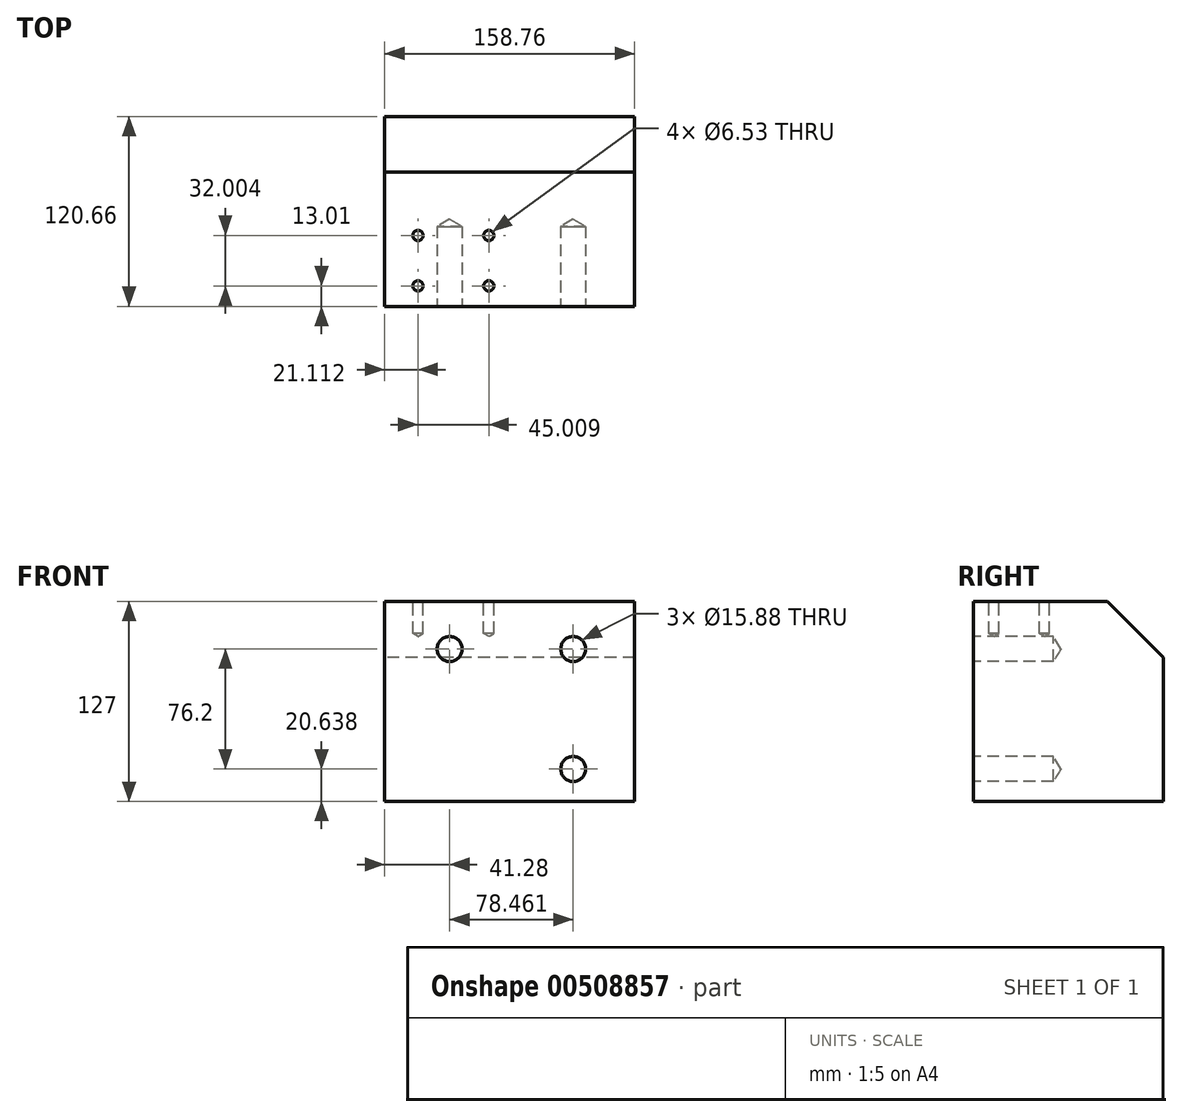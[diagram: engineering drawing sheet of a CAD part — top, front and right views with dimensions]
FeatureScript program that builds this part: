
annotation { "Feature Type Name" : "Feature", "Feature Type Description" : "" }
export const myFeature = defineFeature(function(context is Context, id is Id, definition is map)
    precondition{}
    {
        {
            var Q0;
            Q0=qCreatedBy(makeId("Right.planeOp"),FACE);
            var sketch = newSketch(context, id + "F0", { "sketchPlane" : qUnion([Q0])});
            skLineSegment(sketch, "E0.bottom", {"start": v(24.84, 63.5) * mm, "end": v(-60.32, 63.5) * mm});
            skLineSegment(sketch, "E0.top", {"start": v(60.32, -63.5) * mm, "end": v(-60.33, -63.5) * mm});
            skLineSegment(sketch, "E0.left", {"start": v(60.32, 28.02) * mm, "end": v(60.32, -63.5) * mm});
            skLineSegment(sketch, "E0.right", {"start": v(-60.32, 63.5) * mm, "end": v(-60.33, -63.5) * mm});
            skPoint(sketch, "E0.middle", {"position": v(0, 0) * mm});
            skLineSegment(sketch, "E1", {"start": v(24.84, 63.5) * mm, "end": v(60.32, 28.02) * mm});
            skSolve(sketch);
        }
        {
            var Q0;
            Q0=makeQuery(id+"F0.imprint","IMPRINT",FACE,{"disambiguationData":[TD([[makeQuery(id+"F0.imprint","IMPRINT",EDGE,{"derivedFrom":sQuery(id+"F0.wireOp",EDGE,"E0.bottom")}),1.0]])]});
            extrude(context, id + "F1", {"entities" : qUnion([Q0]), "endBound" : BoundingType.SYMMETRIC, "depth" : 158.75 * mm});
        }
        {
            var Q0;
            Q0=makeQuery(id+"F1.opExtrude","SWEPT_FACE",FACE,{"disambiguationData":[OSD([sQuery(id+"F0.wireOp",EDGE,"E0.right")])]});
            var sketch = newSketch(context, id + "F2", { "sketchPlane" : qUnion([Q0])});
            skPoint(sketch, "E2", {"position": v(40.36, 33.34) * mm});
            skPoint(sketch, "E3", {"position": v(40.36, -42.86) * mm});
            skPoint(sketch, "E4", {"position": v(-38.1, 33.34) * mm});
            skSolve(sketch);
        }
        {
            var Q0;
            Q0=sQuery(id+"F2.wireOp",VERTEX,"E4");
            var Q1;
            Q1=sQuery(id+"F2.wireOp",VERTEX,"E2");
            var Q2;
            Q2=sQuery(id+"F2.wireOp",VERTEX,"E3");
            var Q3;
            Q3=makeQuery(id+"F1.opExtrude","SWEPT_BODY",BODY,{"disambiguationData":[OSD([sQuery(id+"F0.wireOp",EDGE,"E0.bottom"),sQuery(id+"F0.wireOp",EDGE,"E0.top"),sQuery(id+"F0.wireOp",EDGE,"E0.left"),sQuery(id+"F0.wireOp",EDGE,"E0.right"),sQuery(id+"F0.wireOp",EDGE,"E1")])]});
            hole(context, id + "F3", {"style" : HoleStyle.SIMPLE, "endStyle" : HoleEndStyle.BLIND, "holeDiameter" : 15.88 * mm, "holeDepth" : 50.8 * mm, "isTappedThrough" : true, "tappedDepth" : 19.06 * mm, "tapClearance" : 3, "locations" : qUnion([Q0, Q1, Q2]), "scope" : qUnion([Q3])});
        }
        {
            var Q0;
            Q0=makeQuery(id+"F1.opExtrude","SWEPT_FACE",FACE,{"disambiguationData":[OSD([sQuery(id+"F0.wireOp",EDGE,"E0.bottom")])]});
            var sketch = newSketch(context, id + "F4", { "sketchPlane" : qUnion([Q0])});
            skPoint(sketch, "E5", {"position": v(-58.27, -47.32) * mm});
            skPoint(sketch, "E6", {"position": v(-13.26, -47.32) * mm});
            skPoint(sketch, "E7", {"position": v(-13.26, -15.32) * mm});
            skPoint(sketch, "E8", {"position": v(-58.27, -15.32) * mm});
            skSolve(sketch);
        }
        {
            var Q0;
            Q0=sQuery(id+"F4.wireOp",VERTEX,"E8");
            var Q1;
            Q1=sQuery(id+"F4.wireOp",VERTEX,"E5");
            var Q2;
            Q2=sQuery(id+"F4.wireOp",VERTEX,"E6");
            var Q3;
            Q3=sQuery(id+"F4.wireOp",VERTEX,"E7");
            var Q4;
            Q4=makeQuery(id+"F1.opExtrude","SWEPT_BODY",BODY,{"disambiguationData":[OSD([sQuery(id+"F0.wireOp",EDGE,"E0.bottom"),sQuery(id+"F0.wireOp",EDGE,"E0.top"),sQuery(id+"F0.wireOp",EDGE,"E0.left"),sQuery(id+"F0.wireOp",EDGE,"E0.right"),sQuery(id+"F0.wireOp",EDGE,"E1")])]});
            hole(context, id + "F5", {"style" : HoleStyle.SIMPLE, "endStyle" : HoleEndStyle.BLIND, "standardTappedOrClearance" : lookupTablePath({ "standard" : "ANSI", "engagement" : "75%", "pitch" : "18 tpi", "size" : "5/16", "type" : "Tapped" }), "standardBlindInLast" : lookupTablePath({ "standard" : "ANSI", "engagement" : "75%", "pitch" : "18 tpi", "size" : "5/16", "type" : "Tapped" }), "holeDiameter" : 6.53 * mm, "showTappedDepth" : true, "holeDepth" : 20.32 * mm, "isTappedThrough" : true, "tappedDepth" : 16.09 * mm, "tapClearance" : 3, "locations" : qUnion([Q0, Q1, Q2, Q3]), "scope" : qUnion([Q4]), "majorDiameter" : 7.94 * mm});
        }
    });
